# Revit family: Sanitary_Basins_Rak-Ceramics_RAK-MORNING-WASH-BASIN-COUNTER-TOP
name_source: partatom
category: Plumbing Fixtures
revit_build: Autodesk Revit 2015 (Build: 20140606_1530(x64)
units: mm (PartAtom-declared; Revit-internal decimal feet)

## types (1)
- RAK MORNING WASH BASIN COUNTER TOP
    BIMobject category = Basins
    BIMobject category code = sanitary-basins
    BIMobject main category = Sanitary
    BIMobject main category code = sanitary
    Brand url = https://www.rakceramics.com
    Date of publishing = 3/1/2019
    Default Elevation = 1219 mm
    Design country = United Arab Emirates
    Edition number = 1
    IFC Classification = Sanitary Terminal
    Installation instructions = https://www.rakceramics.com
    MEP Diameter = 80 mm
    Manufacturer = Rak Ceramics
    Manufacturer country = United Arab Emirates
    Manufacturer name = Rak Ceramics
    Material main = Ceramics
    Material secondary = Ceramics
    NBS Reference Code = 31-79
    NBS Reference Description = Sinks, Wash Basins And Troughs
    Nominal height = 150 mm
    Nominal width = 540 mm  [stored 1.77165 ft]
    Product Guid = 2988a14b-0ba3-42e0-885f-ae95e5928205
    Product SKU = RAK-MORNING-WASH-BASIN-COUNTER-TOP-54CM-MORCT5400AWHA
    Product certification = https://www.rakceramics.com
    Product data url = https://bimobject.com
    Product family = MORNING
    Product group = Basins
    Product url = https://www.rakceramics.com
    QR code = http://bimobject.com
    Technical description = https://www.rakceramics.com
    Uniclass 1.4 Code = L7212
    Uniclass 1.4 Description = Washbasins
    Uniclass 2.0 Code = PR-31-79
    Uniclass 2.0 Description = Sinks, Wash Basins And Troughs
    Uniclass 2015 Code = Pr_40_20_96
    Uniclass 2015 Name = Wash basins, sinks and troughs
    Weight Net (Kg) = 9
    Youtube clip = https://www.rakceramics.com

note: [stored X ft] marks values corroborated as IEEE doubles in the binary element streams (Revit-internal decimal feet)

## geometry (parser evidence)
native form markers: Sweep x3
no freeform markers — native parametric forms only
